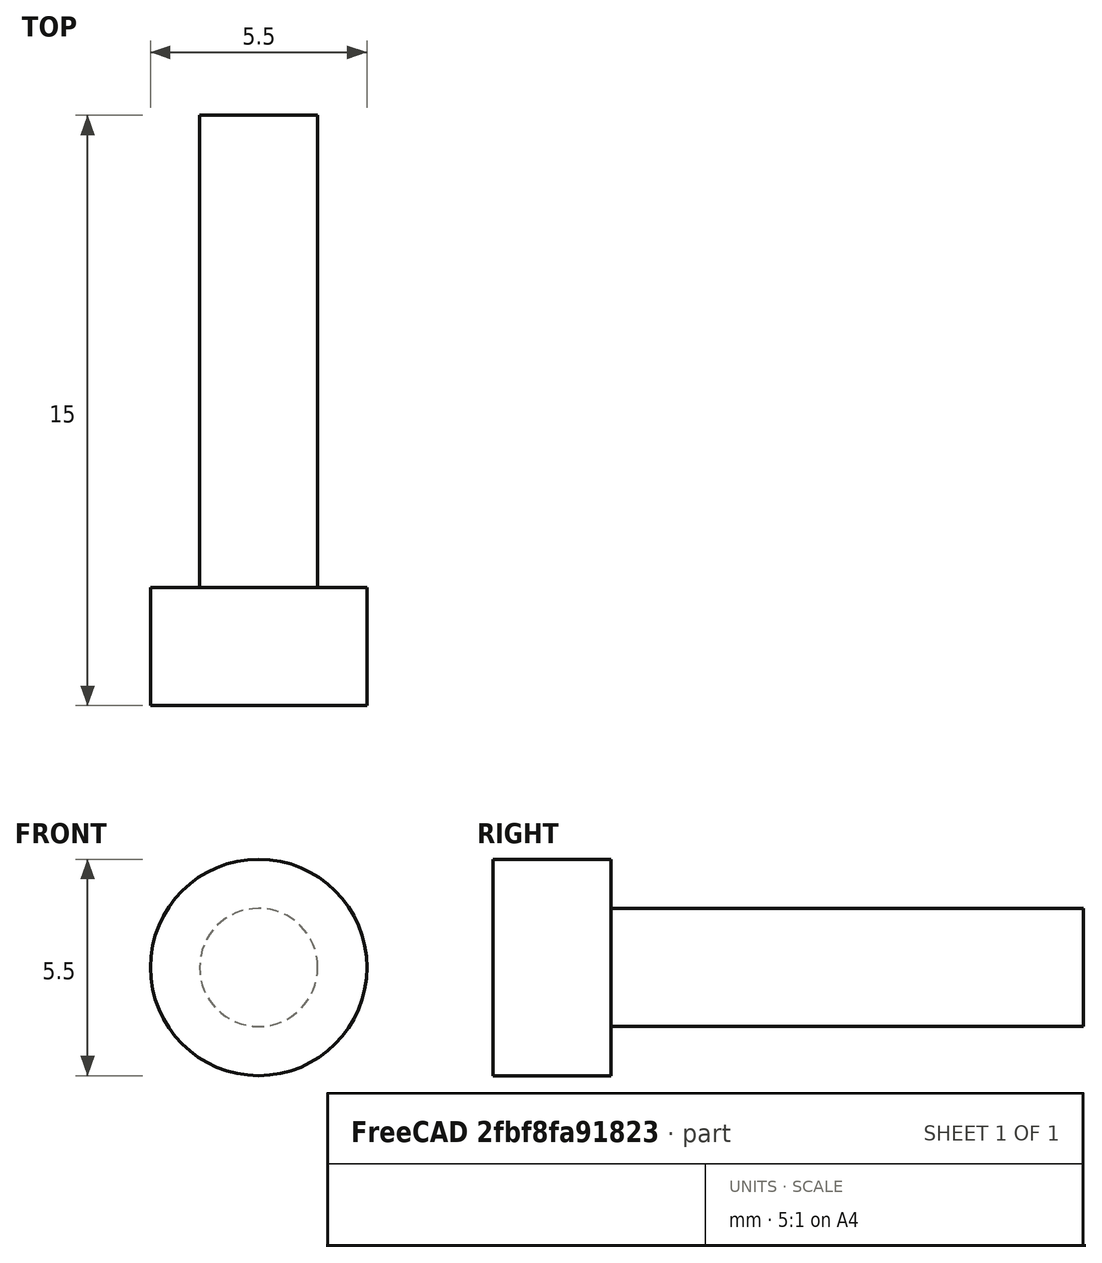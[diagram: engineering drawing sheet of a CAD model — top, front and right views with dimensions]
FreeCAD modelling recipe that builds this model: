
FCSTD DOCUMENT  (FreeCAD 1.0R39319 (Git))
Label: visM3L12
License: All rights reserved
LicenseURL: https://en.wikipedia.org/wiki/All_rights_reserved
objects: Sketcher::SketchObject×1, PartDesign::Revolution×1, PartDesign::Body×1
note: 6 computed .brp shape members not serialized (recipe doc carries the construction recipe); baked Part::Feature solids carry a one-line shape summary decoded from their .brp

FEATURE [Sketcher::SketchObject] Sketch
  ArcFitTolerance = 1e-06
  AttachmentSupport = -> [YZ_Plane]
  FullyConstrained = true
  MakeInternals = false
  MapMode = 5
  Placement = pos=(0,0,0) rot=(0.57735,0.57735,0.57735;2.0944rad)
  sketch-geometry (6):
    g0: LineSegment StartX=-3 StartY=0 StartZ=0 EndX=-3 EndY=2.75 EndZ=0
    g1: LineSegment StartX=-3 StartY=2.75 StartZ=0 EndX=0 EndY=2.75 EndZ=0
    g2: LineSegment StartX=0 StartY=2.75 StartZ=0 EndX=0 EndY=1.5 EndZ=0
    g3: LineSegment StartX=0 StartY=1.5 StartZ=0 EndX=12 EndY=1.5 EndZ=0
    g4: LineSegment StartX=12 StartY=0 StartZ=0 EndX=12 EndY=1.5 EndZ=0
    g5: LineSegment StartX=-3 StartY=0 StartZ=0 EndX=12 EndY=0 EndZ=0
  constraints (18):
    c: PointOnObject(g0,g-1)
    c: Vertical(g0)
    c: Coincident(g1,g0)
    c: PointOnObject(g1,g-2)
    c: Horizontal(g1)
    c: Coincident(g2,g1)
    c: PointOnObject(g2,g-2)
    c: Coincident(g3,g2)
    c: Horizontal(g3)
    c: PointOnObject(g4,g-1)
    c: Coincident(g5,g0)
    c: Coincident(g5,g4)
    c: Coincident(g4,g3)
    c: Perpendicular(g-1,g4)
    c: DistanceY(g0,g0) = 2.75
    c: DistanceX(g1,g1) = 3
    c: DistanceX(g3,g3) = 12
    c: DistanceY(g4,g4) = 1.5
FEATURE [PartDesign::Revolution] Revolution
  Angle = 360
  Angle2 = 60
  Axis = (1e-16,1,-1e-16)
  Base = (0,0,0)
  Placement = pos=(0,0,0) rot=(1,1,1;2.0944rad)
  Profile = -> Sketch
  ReferenceAxis = -> Y_Axis
  Refine = true
  Suppressed = false
  Type = 0
FEATURE [PartDesign::Body] Body  label="Corps"
  AllowCompound = false
  Group = -> [Sketch,Revolution]
  Origin = -> Origin
  Tip = -> Revolution
